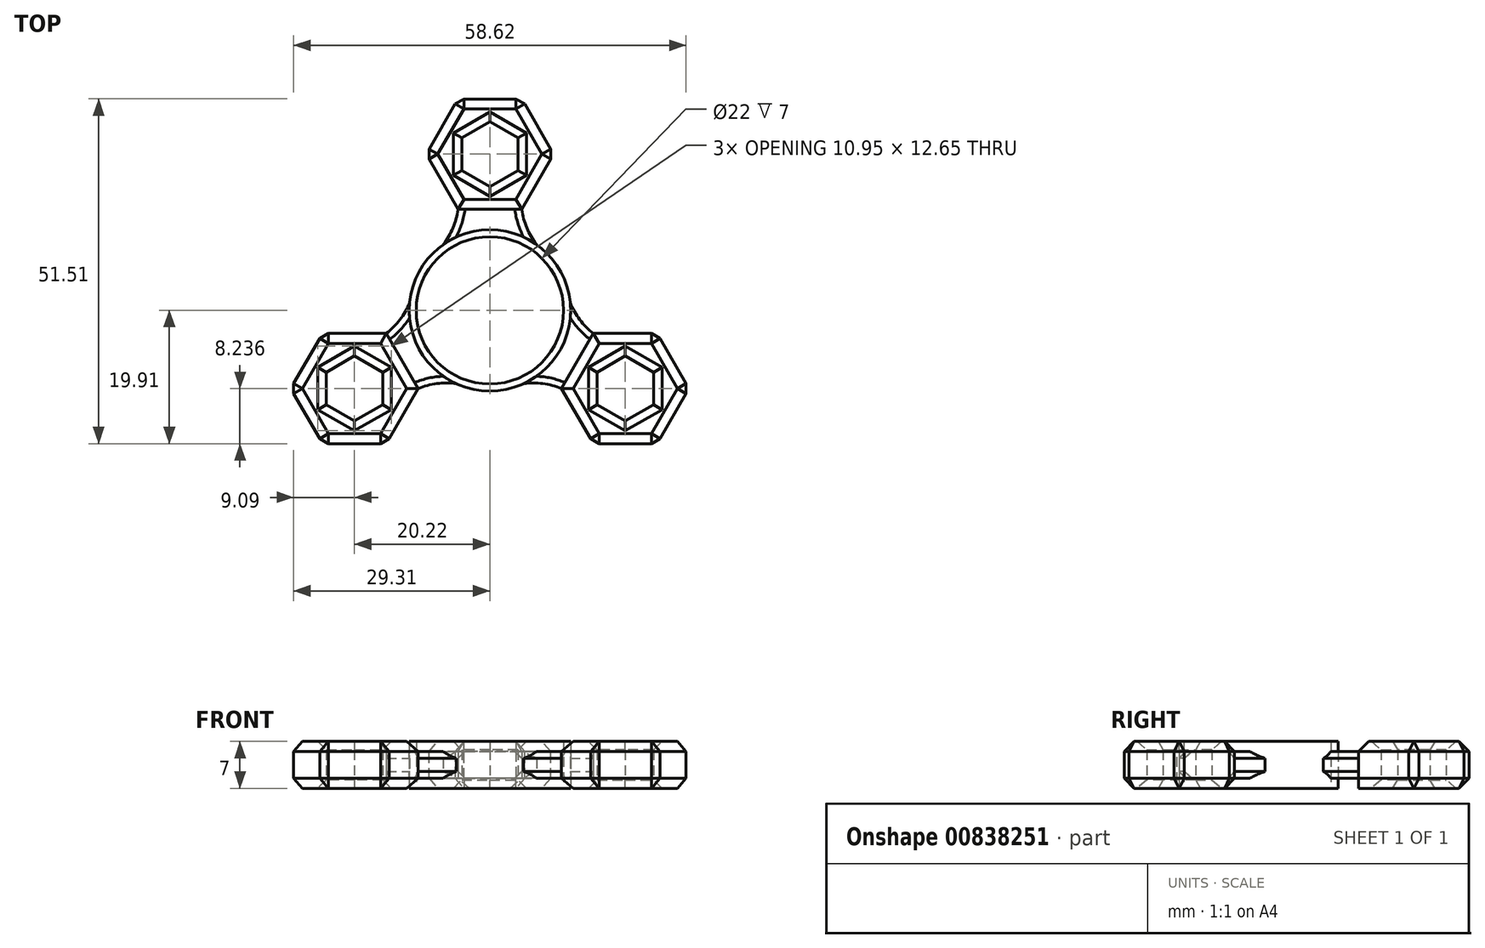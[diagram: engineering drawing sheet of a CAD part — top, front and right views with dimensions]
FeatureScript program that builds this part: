
annotation { "Feature Type Name" : "Feature", "Feature Type Description" : "" }
export const myFeature = defineFeature(function(context is Context, id is Id, definition is map)
    precondition{}
    {
        {
            var Q0;
            Q0=qCreatedBy(makeId("Top.planeOp"),FACE);
            var sketch = newSketch(context, id + "F0", { "sketchPlane" : qUnion([Q0])});
            skLineSegment(sketch, "E0", {"start": v(0, 31.6) * mm, "end": v(4.75, 31.6) * mm});
            skLineSegment(sketch, "E1.MirrorCS", {"start": v(0, 31.6) * mm, "end": v(-4.75, 31.6) * mm});
            skLineSegment(sketch, "E2", {"start": v(4.75, 31.6) * mm, "end": v(9.52, 23.35) * mm});
            skLineSegment(sketch, "E3.MirrorCS", {"start": v(-4.75, 31.6) * mm, "end": v(-9.52, 23.35) * mm});
            skLineSegment(sketch, "E4", {"start": v(9.52, 23.35) * mm, "end": v(4.75, 15.1) * mm});
            skLineSegment(sketch, "E5.MirrorCS", {"start": v(-9.52, 23.35) * mm, "end": v(-4.75, 15.1) * mm});
            skLineSegment(sketch, "E6.MirrorCS", {"start": v(0, 15.1) * mm, "end": v(4.75, 15.1) * mm});
            skLineSegment(sketch, "E7.MirrorCS", {"start": v(0, 15.1) * mm, "end": v(-4.75, 15.1) * mm});
            skLineSegment(sketch, "E8.MirrorCS", {"start": v(-13.08, -7.55) * mm, "end": v(-10.7, -11.67) * mm});
            skLineSegment(sketch, "E9.MirrorCS", {"start": v(-13.08, -7.55) * mm, "end": v(-15.45, -3.43) * mm});
            skLineSegment(sketch, "E10.MirrorCS", {"start": v(-24.98, -3.43) * mm, "end": v(-15.44, -3.43) * mm});
            skLineSegment(sketch, "E11.MirrorCS", {"start": v(-15.46, -19.91) * mm, "end": v(-10.7, -11.66) * mm});
            skLineSegment(sketch, "E12.MirrorCS", {"start": v(-24.99, -19.91) * mm, "end": v(-15.46, -19.91) * mm});
            skLineSegment(sketch, "E13.MirrorCS", {"start": v(-29.74, -11.68) * mm, "end": v(-24.98, -3.43) * mm});
            skLineSegment(sketch, "E14.MirrorCS", {"start": v(-27.36, -15.8) * mm, "end": v(-29.74, -11.68) * mm});
            skLineSegment(sketch, "E15.MirrorCS", {"start": v(-27.36, -15.8) * mm, "end": v(-24.99, -19.91) * mm});
            skLineSegment(sketch, "E16.MirrorCS", {"start": v(13.08, -7.55) * mm, "end": v(15.45, -3.43) * mm});
            skLineSegment(sketch, "E17.MirrorCS", {"start": v(13.08, -7.55) * mm, "end": v(10.7, -11.67) * mm});
            skLineSegment(sketch, "E18.MirrorCS", {"start": v(15.46, -19.91) * mm, "end": v(10.7, -11.66) * mm});
            skLineSegment(sketch, "E19.MirrorCS", {"start": v(24.98, -3.43) * mm, "end": v(15.44, -3.43) * mm});
            skLineSegment(sketch, "E20.MirrorCS", {"start": v(29.74, -11.68) * mm, "end": v(24.98, -3.43) * mm});
            skLineSegment(sketch, "E21.MirrorCS", {"start": v(27.36, -15.8) * mm, "end": v(29.74, -11.68) * mm});
            skLineSegment(sketch, "E22.MirrorCS", {"start": v(27.36, -15.8) * mm, "end": v(24.99, -19.91) * mm});
            skLineSegment(sketch, "E23.MirrorCS", {"start": v(24.99, -19.91) * mm, "end": v(15.46, -19.91) * mm});
            skLineSegment(sketch, "E24.0", {"start": v(-4.2, 25.78) * mm, "end": v(0, 28.2) * mm});
            skLineSegment(sketch, "E24.1", {"start": v(0, 28.2) * mm, "end": v(4.2, 25.78) * mm});
            skLineSegment(sketch, "E24.2", {"start": v(4.2, 25.78) * mm, "end": v(4.2, 20.92) * mm});
            skLineSegment(sketch, "E24.3", {"start": v(4.2, 20.92) * mm, "end": v(0, 18.5) * mm});
            skLineSegment(sketch, "E24.4", {"start": v(0, 18.5) * mm, "end": v(-4.2, 20.92) * mm});
            skLineSegment(sketch, "E24.5", {"start": v(-4.2, 20.92) * mm, "end": v(-4.2, 25.78) * mm});
            skPoint(sketch, "E24.0.midPoint", {"position": v(-2.1, 27) * mm});
            skLineSegment(sketch, "E25.MirrorCS", {"start": v(-16.01, -14.1) * mm, "end": v(-16.01, -9.25) * mm});
            skLineSegment(sketch, "E26.MirrorCS", {"start": v(-16.01, -9.25) * mm, "end": v(-20.22, -6.82) * mm});
            skLineSegment(sketch, "E27.MirrorCS", {"start": v(-20.22, -6.82) * mm, "end": v(-24.43, -9.25) * mm});
            skLineSegment(sketch, "E28.MirrorCS", {"start": v(-24.43, -9.25) * mm, "end": v(-24.43, -14.1) * mm});
            skLineSegment(sketch, "E29.MirrorCS", {"start": v(-24.43, -14.1) * mm, "end": v(-20.22, -16.53) * mm});
            skLineSegment(sketch, "E30.MirrorCS", {"start": v(-20.22, -16.53) * mm, "end": v(-16.01, -14.1) * mm});
            skLineSegment(sketch, "E31.MirrorCS", {"start": v(16.01, -9.25) * mm, "end": v(20.22, -6.82) * mm});
            skLineSegment(sketch, "E32.MirrorCS", {"start": v(16.01, -14.1) * mm, "end": v(16.01, -9.25) * mm});
            skLineSegment(sketch, "E33.MirrorCS", {"start": v(20.22, -16.53) * mm, "end": v(16.01, -14.1) * mm});
            skLineSegment(sketch, "E34.MirrorCS", {"start": v(24.43, -14.1) * mm, "end": v(20.22, -16.53) * mm});
            skLineSegment(sketch, "E35.MirrorCS", {"start": v(24.43, -9.25) * mm, "end": v(24.43, -14.1) * mm});
            skLineSegment(sketch, "E36.MirrorCS", {"start": v(20.22, -6.82) * mm, "end": v(24.43, -9.25) * mm});
            skCircle(sketch, "E37", {"center": v(0, 0) * mm, "radius": 11 * mm});
            skCircle(sketch, "E38", {"center": v(0, 0) * mm, "radius": 12.05 * mm});
            skArc(sketch, "E39", {"start": v(4.75, 15.1) * mm, "mid": v(5.52, 12.32) * mm, "end": v(6.97, 9.83) * mm});
            skArc(sketch, "E40.MirrorCS", {"start": v(-4.75, 15.1) * mm, "mid": v(-5.52, 12.32) * mm, "end": v(-6.97, 9.83) * mm});
            skArc(sketch, "E41.MirrorCS", {"start": v(-10.7, -11.67) * mm, "mid": v(-7.91, -10.94) * mm, "end": v(-5.03, -10.95) * mm});
            skArc(sketch, "E42.MirrorCS", {"start": v(-15.45, -3.43) * mm, "mid": v(-13.43, -1.38) * mm, "end": v(-12, 1.12) * mm});
            skArc(sketch, "E43.MirrorCS", {"start": v(15.45, -3.43) * mm, "mid": v(13.43, -1.38) * mm, "end": v(12, 1.12) * mm});
            skArc(sketch, "E44.MirrorCS", {"start": v(10.7, -11.67) * mm, "mid": v(7.91, -10.94) * mm, "end": v(5.03, -10.95) * mm});
            skSolve(sketch);
        }
        {
            var Q0;
            Q0=makeQuery(id+"F0.imprint","IMPRINT",FACE,{"disambiguationData":[TD([[makeQuery(id+"F0.imprint","IMPRINT",EDGE,{"derivedFrom":sQuery(id+"F0.wireOp",EDGE,"E0")}),-1.0]])]});
            var Q1;
            {var subQ4=sQuery(id+"F0.wireOp",EDGE,"E16.MirrorCS");Q1=makeQuery(id+"F0.imprint","IMPRINT",FACE,{"disambiguationData":[TD([[makeQuery(id+"F0.imprint","IMPRINT",EDGE,{"derivedFrom":subQ4}),-1.0]])]});}
            var Q2;
            {var subQ2=sQuery(id+"F0.wireOp",EDGE,"E8.MirrorCS");Q2=makeQuery(id+"F0.imprint","IMPRINT",FACE,{"disambiguationData":[TD([[makeQuery(id+"F0.imprint","IMPRINT",EDGE,{"derivedFrom":subQ2}),-1.0]])]});}
            var Q3;
            Q3=makeQuery(id+"F0.imprint","IMPRINT",FACE,{"disambiguationData":[TD([[makeQuery(id+"F0.imprint","IMPRINT",EDGE,{"derivedFrom":sQuery(id+"F0.wireOp",EDGE,"xe7wqnzr-XKuB-rW0O-xTz1-b7jerHm42rLD")}),-1.0]])]});
            extrude(context, id + "F1", {"entities" : qUnion([Q0, Q1, Q2, Q3]), "depth" : 7 * mm, "offsetDistance" : 25.4 * mm});
        }
        {
            var Q0;
            Q0=makeQuery(id+"F0.imprint","IMPRINT",FACE,{"disambiguationData":[TD([[makeQuery(id+"F0.imprint","IMPRINT",EDGE,{"derivedFrom":sQuery(id+"F0.wireOp",EDGE,"E16.MirrorCS")}),1.0]])]});
            var Q1;
            Q1=makeQuery(id+"F0.imprint","IMPRINT",FACE,{"disambiguationData":[TD([[makeQuery(id+"F0.imprint","IMPRINT",EDGE,{"derivedFrom":sQuery(id+"F0.wireOp",EDGE,"E8.MirrorCS")}),1.0]])]});
            var Q2;
            Q2=makeQuery(id+"F0.imprint","IMPRINT",FACE,{"disambiguationData":[TD([[makeQuery(id+"F0.imprint","IMPRINT",EDGE,{"derivedFrom":sQuery(id+"F0.wireOp",EDGE,"E6.MirrorCS")}),-1.0]])]});
            extrude(context, id + "F2", {"entities" : qUnion([Q0, Q1, Q2]), "depth" : 4 * mm, "offsetDistance" : 25.4 * mm});
        }
        {
            var Q0;
            Q0=makeQuery(id+"F2.opExtrude","SWEPT_BODY",BODY,{"disambiguationData":[OSD([sQuery(id+"F0.wireOp",EDGE,"vPjK45c8-EVP7-AFoe-6fc5-zKXZbxQBUroo"),sQuery(id+"F0.wireOp",EDGE,"E8.MirrorCS"),sQuery(id+"F0.wireOp",EDGE,"E9.MirrorCS"),sQuery(id+"F0.wireOp",EDGE,"01c6eca7-8cec-47bf-bf10-1e8c1c321e7b0.MirrorCS"),sQuery(id+"F0.wireOp",EDGE,"d1bce0d9-914a-43dd-a102-95f5fd3e93660.MirrorCS")])]});
            var Q1;
            Q1=makeQuery(id+"F2.opExtrude","SWEPT_BODY",BODY,{"disambiguationData":[OSD([sQuery(id+"F0.wireOp",EDGE,"vPjK45c8-EVP7-AFoe-6fc5-zKXZbxQBUroo"),sQuery(id+"F0.wireOp",EDGE,"E6.MirrorCS"),sQuery(id+"F0.wireOp",EDGE,"E7.MirrorCS"),sQuery(id+"F0.wireOp",EDGE,"E15wmxCf-tLpu-X0cc-KYuK-EZGoAjTdYror"),sQuery(id+"F0.wireOp",EDGE,"b77f33ba-465c-4afd-8519-29dd17539a6f0.MirrorCS")])]});
            var Q2;
            Q2=makeQuery(id+"F2.opExtrude","SWEPT_BODY",BODY,{"disambiguationData":[OSD([sQuery(id+"F0.wireOp",EDGE,"vPjK45c8-EVP7-AFoe-6fc5-zKXZbxQBUroo"),sQuery(id+"F0.wireOp",EDGE,"E16.MirrorCS"),sQuery(id+"F0.wireOp",EDGE,"E17.MirrorCS"),sQuery(id+"F0.wireOp",EDGE,"b3ed12b7-8768-48b8-8f4e-18517871a5bf0.MirrorCS"),sQuery(id+"F0.wireOp",EDGE,"d635de01-bb5d-4376-a8ab-b6ab56e229920.MirrorCS")])]});
            transform(context, id + "F3", {"entities" : qUnion([Q0, Q1, Q2]), "transformType" : TransformType.TRANSLATION_3D, "dx" : 0 * mm, "dy" : 0 * mm, "dz" : 1.5 * mm, "makeCopy" : false});
        }
        {
            var Q0;
            Q0=makeQuery(id+"F2.opExtrude","CAP_EDGE",EDGE,{"disambiguationData":[OSD([sQuery(id+"F0.wireOp",EDGE,"b77f33ba-465c-4afd-8519-29dd17539a6f0.MirrorCS")])],"isStart":false});
            var Q1;
            Q1=makeQuery(id+"F2.opExtrude","CAP_EDGE",EDGE,{"disambiguationData":[OSD([sQuery(id+"F0.wireOp",EDGE,"b77f33ba-465c-4afd-8519-29dd17539a6f0.MirrorCS")])],"isStart":true});
            var Q2;
            Q2=makeQuery(id+"F2.opExtrude","CAP_EDGE",EDGE,{"disambiguationData":[OSD([sQuery(id+"F0.wireOp",EDGE,"E15wmxCf-tLpu-X0cc-KYuK-EZGoAjTdYror")])],"isStart":false});
            var Q3;
            Q3=makeQuery(id+"F2.opExtrude","CAP_EDGE",EDGE,{"disambiguationData":[OSD([sQuery(id+"F0.wireOp",EDGE,"E15wmxCf-tLpu-X0cc-KYuK-EZGoAjTdYror")])],"isStart":true});
            var Q4;
            Q4=makeQuery(id+"F2.opExtrude","CAP_EDGE",EDGE,{"disambiguationData":[OSD([sQuery(id+"F0.wireOp",EDGE,"b3ed12b7-8768-48b8-8f4e-18517871a5bf0.MirrorCS")])],"isStart":true});
            var Q5;
            Q5=makeQuery(id+"F2.opExtrude","CAP_EDGE",EDGE,{"disambiguationData":[OSD([sQuery(id+"F0.wireOp",EDGE,"b3ed12b7-8768-48b8-8f4e-18517871a5bf0.MirrorCS")])],"isStart":false});
            var Q6;
            Q6=makeQuery(id+"F2.opExtrude","CAP_EDGE",EDGE,{"disambiguationData":[OSD([sQuery(id+"F0.wireOp",EDGE,"d635de01-bb5d-4376-a8ab-b6ab56e229920.MirrorCS")])],"isStart":false});
            var Q7;
            Q7=makeQuery(id+"F2.opExtrude","CAP_EDGE",EDGE,{"disambiguationData":[OSD([sQuery(id+"F0.wireOp",EDGE,"d635de01-bb5d-4376-a8ab-b6ab56e229920.MirrorCS")])],"isStart":true});
            var Q8;
            Q8=makeQuery(id+"F2.opExtrude","CAP_EDGE",EDGE,{"disambiguationData":[OSD([sQuery(id+"F0.wireOp",EDGE,"01c6eca7-8cec-47bf-bf10-1e8c1c321e7b0.MirrorCS")])],"isStart":true});
            var Q9;
            Q9=makeQuery(id+"F2.opExtrude","CAP_EDGE",EDGE,{"disambiguationData":[OSD([sQuery(id+"F0.wireOp",EDGE,"01c6eca7-8cec-47bf-bf10-1e8c1c321e7b0.MirrorCS")])],"isStart":false});
            var Q10;
            Q10=makeQuery(id+"F2.opExtrude","CAP_EDGE",EDGE,{"disambiguationData":[OSD([sQuery(id+"F0.wireOp",EDGE,"d1bce0d9-914a-43dd-a102-95f5fd3e93660.MirrorCS")])],"isStart":true});
            var Q11;
            Q11=makeQuery(id+"F2.opExtrude","CAP_EDGE",EDGE,{"disambiguationData":[OSD([sQuery(id+"F0.wireOp",EDGE,"d1bce0d9-914a-43dd-a102-95f5fd3e93660.MirrorCS")])],"isStart":false});
            var Q12;
            Q12=makeQuery(id+"F1.opExtrude","CAP_EDGE",EDGE,{"disambiguationData":[OSD([sQuery(id+"F0.wireOp",EDGE,"E16.MirrorCS"),sQuery(id+"F0.wireOp",EDGE,"E17.MirrorCS")])],"isStart":false});
            var Q13;
            Q13=makeQuery(id+"F1.opExtrude","CAP_EDGE",EDGE,{"disambiguationData":[OSD([sQuery(id+"F0.wireOp",EDGE,"E18.MirrorCS")])],"isStart":false});
            var Q14;
            Q14=makeQuery(id+"F1.opExtrude","CAP_EDGE",EDGE,{"disambiguationData":[OSD([sQuery(id+"F0.wireOp",EDGE,"E23.MirrorCS")])],"isStart":false});
            var Q15;
            Q15=makeQuery(id+"F1.opExtrude","CAP_EDGE",EDGE,{"disambiguationData":[OSD([sQuery(id+"F0.wireOp",EDGE,"E21.MirrorCS"),sQuery(id+"F0.wireOp",EDGE,"E22.MirrorCS")])],"isStart":false});
            var Q16;
            Q16=makeQuery(id+"F1.opExtrude","CAP_EDGE",EDGE,{"disambiguationData":[OSD([sQuery(id+"F0.wireOp",EDGE,"E19.MirrorCS")])],"isStart":false});
            var Q17;
            Q17=makeQuery(id+"F1.opExtrude","CAP_EDGE",EDGE,{"disambiguationData":[OSD([sQuery(id+"F0.wireOp",EDGE,"E20.MirrorCS")])],"isStart":false});
            var Q18;
            Q18=makeQuery(id+"F1.opExtrude","CAP_EDGE",EDGE,{"disambiguationData":[OSD([sQuery(id+"F0.wireOp",EDGE,"E4")])],"isStart":false});
            var Q19;
            Q19=makeQuery(id+"F1.opExtrude","CAP_EDGE",EDGE,{"disambiguationData":[OSD([sQuery(id+"F0.wireOp",EDGE,"E2")])],"isStart":false});
            var Q20;
            Q20=makeQuery(id+"F1.opExtrude","CAP_EDGE",EDGE,{"disambiguationData":[OSD([sQuery(id+"F0.wireOp",EDGE,"E6.MirrorCS"),sQuery(id+"F0.wireOp",EDGE,"E7.MirrorCS")])],"isStart":false});
            var Q21;
            Q21=makeQuery(id+"F1.opExtrude","CAP_EDGE",EDGE,{"disambiguationData":[OSD([sQuery(id+"F0.wireOp",EDGE,"E5.MirrorCS")])],"isStart":false});
            var Q22;
            Q22=makeQuery(id+"F1.opExtrude","CAP_EDGE",EDGE,{"disambiguationData":[OSD([sQuery(id+"F0.wireOp",EDGE,"E3.MirrorCS")])],"isStart":false});
            var Q23;
            Q23=makeQuery(id+"F1.opExtrude","CAP_EDGE",EDGE,{"disambiguationData":[OSD([sQuery(id+"F0.wireOp",EDGE,"E0"),sQuery(id+"F0.wireOp",EDGE,"E1.MirrorCS")])],"isStart":false});
            var Q24;
            Q24=makeQuery(id+"F1.opExtrude","CAP_EDGE",EDGE,{"disambiguationData":[OSD([sQuery(id+"F0.wireOp",EDGE,"E10.MirrorCS")])],"isStart":false});
            var Q25;
            Q25=makeQuery(id+"F1.opExtrude","CAP_EDGE",EDGE,{"disambiguationData":[OSD([sQuery(id+"F0.wireOp",EDGE,"E13.MirrorCS")])],"isStart":false});
            var Q26;
            Q26=makeQuery(id+"F1.opExtrude","CAP_EDGE",EDGE,{"disambiguationData":[OSD([sQuery(id+"F0.wireOp",EDGE,"E14.MirrorCS"),sQuery(id+"F0.wireOp",EDGE,"E15.MirrorCS")])],"isStart":false});
            var Q27;
            Q27=makeQuery(id+"F1.opExtrude","CAP_EDGE",EDGE,{"disambiguationData":[OSD([sQuery(id+"F0.wireOp",EDGE,"E12.MirrorCS")])],"isStart":false});
            var Q28;
            Q28=makeQuery(id+"F1.opExtrude","CAP_EDGE",EDGE,{"disambiguationData":[OSD([sQuery(id+"F0.wireOp",EDGE,"E11.MirrorCS")])],"isStart":false});
            var Q29;
            Q29=makeQuery(id+"F1.opExtrude","CAP_EDGE",EDGE,{"disambiguationData":[OSD([sQuery(id+"F0.wireOp",EDGE,"E8.MirrorCS"),sQuery(id+"F0.wireOp",EDGE,"E9.MirrorCS")])],"isStart":false});
            var Q30;
            Q30=makeQuery(id+"F1.opExtrude","CAP_EDGE",EDGE,{"disambiguationData":[OSD([sQuery(id+"F0.wireOp",EDGE,"E18.MirrorCS")])],"isStart":true});
            var Q31;
            Q31=makeQuery(id+"F1.opExtrude","CAP_EDGE",EDGE,{"disambiguationData":[OSD([sQuery(id+"F0.wireOp",EDGE,"E23.MirrorCS")])],"isStart":true});
            var Q32;
            Q32=makeQuery(id+"F1.opExtrude","CAP_EDGE",EDGE,{"disambiguationData":[OSD([sQuery(id+"F0.wireOp",EDGE,"E16.MirrorCS"),sQuery(id+"F0.wireOp",EDGE,"E17.MirrorCS")])],"isStart":true});
            var Q33;
            Q33=makeQuery(id+"F1.opExtrude","CAP_EDGE",EDGE,{"disambiguationData":[OSD([sQuery(id+"F0.wireOp",EDGE,"E21.MirrorCS"),sQuery(id+"F0.wireOp",EDGE,"E22.MirrorCS")])],"isStart":true});
            var Q34;
            Q34=makeQuery(id+"F1.opExtrude","CAP_EDGE",EDGE,{"disambiguationData":[OSD([sQuery(id+"F0.wireOp",EDGE,"E20.MirrorCS")])],"isStart":true});
            var Q35;
            Q35=makeQuery(id+"F1.opExtrude","CAP_EDGE",EDGE,{"disambiguationData":[OSD([sQuery(id+"F0.wireOp",EDGE,"E19.MirrorCS")])],"isStart":true});
            var Q36;
            Q36=makeQuery(id+"F1.opExtrude","SWEPT_EDGE",EDGE,{"disambiguationData":[OSD([sQuery(id+"F0.wireOp",EDGE,"E23.MirrorCS"),sQuery(id+"F0.wireOp",EDGE,"E18.MirrorCS")])]});
            var Q37;
            Q37=makeQuery(id+"F1.opExtrude","SWEPT_EDGE",EDGE,{"disambiguationData":[OSD([sQuery(id+"F0.wireOp",EDGE,"E22.MirrorCS"),sQuery(id+"F0.wireOp",EDGE,"E23.MirrorCS")])]});
            var Q38;
            Q38=makeQuery(id+"F1.opExtrude","SWEPT_EDGE",EDGE,{"disambiguationData":[OSD([sQuery(id+"F0.wireOp",EDGE,"E20.MirrorCS"),sQuery(id+"F0.wireOp",EDGE,"E21.MirrorCS")])]});
            var Q39;
            Q39=makeQuery(id+"F1.opExtrude","SWEPT_EDGE",EDGE,{"disambiguationData":[OSD([sQuery(id+"F0.wireOp",EDGE,"E19.MirrorCS"),sQuery(id+"F0.wireOp",EDGE,"E20.MirrorCS")])]});
            var Q40;
            Q40=makeQuery(id+"F1.opExtrude","CAP_EDGE",EDGE,{"disambiguationData":[OSD([sQuery(id+"F0.wireOp",EDGE,"E8.MirrorCS"),sQuery(id+"F0.wireOp",EDGE,"E9.MirrorCS")])],"isStart":true});
            var Q41;
            Q41=makeQuery(id+"F1.opExtrude","CAP_EDGE",EDGE,{"disambiguationData":[OSD([sQuery(id+"F0.wireOp",EDGE,"E11.MirrorCS")])],"isStart":true});
            var Q42;
            Q42=makeQuery(id+"F1.opExtrude","CAP_EDGE",EDGE,{"disambiguationData":[OSD([sQuery(id+"F0.wireOp",EDGE,"E12.MirrorCS")])],"isStart":true});
            var Q43;
            Q43=makeQuery(id+"F1.opExtrude","CAP_EDGE",EDGE,{"disambiguationData":[OSD([sQuery(id+"F0.wireOp",EDGE,"E14.MirrorCS"),sQuery(id+"F0.wireOp",EDGE,"E15.MirrorCS")])],"isStart":true});
            var Q44;
            Q44=makeQuery(id+"F1.opExtrude","CAP_EDGE",EDGE,{"disambiguationData":[OSD([sQuery(id+"F0.wireOp",EDGE,"E13.MirrorCS")])],"isStart":true});
            var Q45;
            Q45=makeQuery(id+"F1.opExtrude","CAP_EDGE",EDGE,{"disambiguationData":[OSD([sQuery(id+"F0.wireOp",EDGE,"E10.MirrorCS")])],"isStart":true});
            var Q46;
            Q46=makeQuery(id+"F1.opExtrude","SWEPT_EDGE",EDGE,{"disambiguationData":[OSD([sQuery(id+"F0.wireOp",EDGE,"E11.MirrorCS"),sQuery(id+"F0.wireOp",EDGE,"E12.MirrorCS")])]});
            var Q47;
            Q47=makeQuery(id+"F1.opExtrude","SWEPT_EDGE",EDGE,{"disambiguationData":[OSD([sQuery(id+"F0.wireOp",EDGE,"E12.MirrorCS"),sQuery(id+"F0.wireOp",EDGE,"E15.MirrorCS")])]});
            var Q48;
            Q48=makeQuery(id+"F1.opExtrude","SWEPT_EDGE",EDGE,{"disambiguationData":[OSD([sQuery(id+"F0.wireOp",EDGE,"E13.MirrorCS"),sQuery(id+"F0.wireOp",EDGE,"E14.MirrorCS")])]});
            var Q49;
            Q49=makeQuery(id+"F1.opExtrude","SWEPT_EDGE",EDGE,{"disambiguationData":[OSD([sQuery(id+"F0.wireOp",EDGE,"E3.MirrorCS"),sQuery(id+"F0.wireOp",EDGE,"E5.MirrorCS")])]});
            var Q50;
            Q50=makeQuery(id+"F1.opExtrude","SWEPT_EDGE",EDGE,{"disambiguationData":[OSD([sQuery(id+"F0.wireOp",EDGE,"E1.MirrorCS"),sQuery(id+"F0.wireOp",EDGE,"E3.MirrorCS")])]});
            var Q51;
            Q51=makeQuery(id+"F1.opExtrude","SWEPT_EDGE",EDGE,{"disambiguationData":[OSD([sQuery(id+"F0.wireOp",EDGE,"E0"),sQuery(id+"F0.wireOp",EDGE,"E2")])]});
            var Q52;
            Q52=makeQuery(id+"F1.opExtrude","CAP_EDGE",EDGE,{"disambiguationData":[OSD([sQuery(id+"F0.wireOp",EDGE,"E0"),sQuery(id+"F0.wireOp",EDGE,"E1.MirrorCS")])],"isStart":true});
            var Q53;
            Q53=makeQuery(id+"F1.opExtrude","CAP_EDGE",EDGE,{"disambiguationData":[OSD([sQuery(id+"F0.wireOp",EDGE,"E3.MirrorCS")])],"isStart":true});
            var Q54;
            Q54=makeQuery(id+"F1.opExtrude","CAP_EDGE",EDGE,{"disambiguationData":[OSD([sQuery(id+"F0.wireOp",EDGE,"E5.MirrorCS")])],"isStart":true});
            var Q55;
            Q55=makeQuery(id+"F1.opExtrude","SWEPT_EDGE",EDGE,{"disambiguationData":[OSD([sQuery(id+"F0.wireOp",EDGE,"E2"),sQuery(id+"F0.wireOp",EDGE,"E4")])]});
            var Q56;
            Q56=makeQuery(id+"F1.opExtrude","CAP_EDGE",EDGE,{"disambiguationData":[OSD([sQuery(id+"F0.wireOp",EDGE,"E2")])],"isStart":true});
            var Q57;
            Q57=makeQuery(id+"F1.opExtrude","CAP_EDGE",EDGE,{"disambiguationData":[OSD([sQuery(id+"F0.wireOp",EDGE,"E4")])],"isStart":true});
            var Q58;
            Q58=makeQuery(id+"F1.opExtrude","SWEPT_EDGE",EDGE,{"disambiguationData":[OSD([sQuery(id+"F0.wireOp",EDGE,"E10.MirrorCS"),sQuery(id+"F0.wireOp",EDGE,"E13.MirrorCS")])]});
            chamfer(context, id + "F4", {"entities" : qUnion([Q0, Q1, Q2, Q3, Q4, Q5, Q6, Q7, Q8, Q9, Q10, Q11, Q12, Q13, Q14, Q15, Q16, Q17, Q18, Q19, Q20, Q21, Q22, Q23, Q24, Q25, Q26, Q27, Q28, Q29, Q30, Q31, Q32, Q33, Q34, Q35, Q36, Q37, Q38, Q39, Q40, Q41, Q42, Q43, Q44, Q45, Q46, Q47, Q48, Q49, Q50, Q51, Q52, Q53, Q54, Q55, Q56, Q57, Q58]), "width" : 1.5 * mm, "tangentPropagation" : true});
        }
        {
            var Q0;
            Q0=makeQuery(id+"F1.opExtrude","CAP_EDGE",EDGE,{"disambiguationData":[OSD([sQuery(id+"F0.wireOp",EDGE,"E31.MirrorCS")])],"isStart":true});
            var Q1;
            Q1=makeQuery(id+"F1.opExtrude","CAP_EDGE",EDGE,{"disambiguationData":[OSD([sQuery(id+"F0.wireOp",EDGE,"E36.MirrorCS")])],"isStart":true});
            var Q2;
            Q2=makeQuery(id+"F1.opExtrude","CAP_EDGE",EDGE,{"disambiguationData":[OSD([sQuery(id+"F0.wireOp",EDGE,"E31.MirrorCS")])],"isStart":false});
            var Q3;
            Q3=makeQuery(id+"F1.opExtrude","CAP_EDGE",EDGE,{"disambiguationData":[OSD([sQuery(id+"F0.wireOp",EDGE,"E36.MirrorCS")])],"isStart":false});
            var Q4;
            Q4=makeQuery(id+"F1.opExtrude","CAP_EDGE",EDGE,{"disambiguationData":[OSD([sQuery(id+"F0.wireOp",EDGE,"E32.MirrorCS")])],"isStart":true});
            var Q5;
            Q5=makeQuery(id+"F1.opExtrude","CAP_EDGE",EDGE,{"disambiguationData":[OSD([sQuery(id+"F0.wireOp",EDGE,"E32.MirrorCS")])],"isStart":false});
            var Q6;
            Q6=makeQuery(id+"F1.opExtrude","CAP_EDGE",EDGE,{"disambiguationData":[OSD([sQuery(id+"F0.wireOp",EDGE,"E35.MirrorCS")])],"isStart":false});
            var Q7;
            Q7=makeQuery(id+"F1.opExtrude","CAP_EDGE",EDGE,{"disambiguationData":[OSD([sQuery(id+"F0.wireOp",EDGE,"E35.MirrorCS")])],"isStart":true});
            var Q8;
            Q8=makeQuery(id+"F1.opExtrude","CAP_EDGE",EDGE,{"disambiguationData":[OSD([sQuery(id+"F0.wireOp",EDGE,"E34.MirrorCS")])],"isStart":false});
            var Q9;
            Q9=makeQuery(id+"F1.opExtrude","CAP_EDGE",EDGE,{"disambiguationData":[OSD([sQuery(id+"F0.wireOp",EDGE,"E33.MirrorCS")])],"isStart":false});
            var Q10;
            Q10=makeQuery(id+"F1.opExtrude","CAP_EDGE",EDGE,{"disambiguationData":[OSD([sQuery(id+"F0.wireOp",EDGE,"E34.MirrorCS")])],"isStart":true});
            var Q11;
            Q11=makeQuery(id+"F1.opExtrude","CAP_EDGE",EDGE,{"disambiguationData":[OSD([sQuery(id+"F0.wireOp",EDGE,"E33.MirrorCS")])],"isStart":true});
            var Q12;
            Q12=makeQuery(id+"F1.opExtrude","CAP_EDGE",EDGE,{"disambiguationData":[OSD([sQuery(id+"F0.wireOp",EDGE,"E29.MirrorCS")])],"isStart":true});
            var Q13;
            Q13=makeQuery(id+"F1.opExtrude","CAP_EDGE",EDGE,{"disambiguationData":[OSD([sQuery(id+"F0.wireOp",EDGE,"E30.MirrorCS")])],"isStart":true});
            var Q14;
            Q14=makeQuery(id+"F1.opExtrude","CAP_EDGE",EDGE,{"disambiguationData":[OSD([sQuery(id+"F0.wireOp",EDGE,"E25.MirrorCS")])],"isStart":true});
            var Q15;
            Q15=makeQuery(id+"F1.opExtrude","CAP_EDGE",EDGE,{"disambiguationData":[OSD([sQuery(id+"F0.wireOp",EDGE,"E26.MirrorCS")])],"isStart":false});
            var Q16;
            Q16=makeQuery(id+"F1.opExtrude","CAP_EDGE",EDGE,{"disambiguationData":[OSD([sQuery(id+"F0.wireOp",EDGE,"E25.MirrorCS")])],"isStart":false});
            var Q17;
            Q17=makeQuery(id+"F1.opExtrude","CAP_EDGE",EDGE,{"disambiguationData":[OSD([sQuery(id+"F0.wireOp",EDGE,"E30.MirrorCS")])],"isStart":false});
            var Q18;
            Q18=makeQuery(id+"F1.opExtrude","CAP_EDGE",EDGE,{"disambiguationData":[OSD([sQuery(id+"F0.wireOp",EDGE,"E29.MirrorCS")])],"isStart":false});
            var Q19;
            Q19=makeQuery(id+"F1.opExtrude","CAP_EDGE",EDGE,{"disambiguationData":[OSD([sQuery(id+"F0.wireOp",EDGE,"E28.MirrorCS")])],"isStart":true});
            var Q20;
            Q20=makeQuery(id+"F1.opExtrude","CAP_EDGE",EDGE,{"disambiguationData":[OSD([sQuery(id+"F0.wireOp",EDGE,"E28.MirrorCS")])],"isStart":false});
            var Q21;
            Q21=makeQuery(id+"F1.opExtrude","CAP_EDGE",EDGE,{"disambiguationData":[OSD([sQuery(id+"F0.wireOp",EDGE,"E27.MirrorCS")])],"isStart":false});
            var Q22;
            Q22=makeQuery(id+"F1.opExtrude","CAP_EDGE",EDGE,{"disambiguationData":[OSD([sQuery(id+"F0.wireOp",EDGE,"E27.MirrorCS")])],"isStart":true});
            var Q23;
            Q23=makeQuery(id+"F1.opExtrude","CAP_EDGE",EDGE,{"disambiguationData":[OSD([sQuery(id+"F0.wireOp",EDGE,"E26.MirrorCS")])],"isStart":true});
            var Q24;
            Q24=makeQuery(id+"F1.opExtrude","CAP_EDGE",EDGE,{"disambiguationData":[OSD([sQuery(id+"F0.wireOp",EDGE,"E24.0")])],"isStart":true});
            var Q25;
            Q25=makeQuery(id+"F1.opExtrude","CAP_EDGE",EDGE,{"disambiguationData":[OSD([sQuery(id+"F0.wireOp",EDGE,"E24.0")])],"isStart":false});
            var Q26;
            Q26=makeQuery(id+"F1.opExtrude","CAP_EDGE",EDGE,{"disambiguationData":[OSD([sQuery(id+"F0.wireOp",EDGE,"E24.5")])],"isStart":false});
            var Q27;
            Q27=makeQuery(id+"F1.opExtrude","CAP_EDGE",EDGE,{"disambiguationData":[OSD([sQuery(id+"F0.wireOp",EDGE,"E24.5")])],"isStart":true});
            var Q28;
            Q28=makeQuery(id+"F1.opExtrude","CAP_EDGE",EDGE,{"disambiguationData":[OSD([sQuery(id+"F0.wireOp",EDGE,"E24.4")])],"isStart":false});
            var Q29;
            Q29=makeQuery(id+"F1.opExtrude","CAP_EDGE",EDGE,{"disambiguationData":[OSD([sQuery(id+"F0.wireOp",EDGE,"E24.4")])],"isStart":true});
            var Q30;
            Q30=makeQuery(id+"F1.opExtrude","CAP_EDGE",EDGE,{"disambiguationData":[OSD([sQuery(id+"F0.wireOp",EDGE,"E24.1")])],"isStart":true});
            var Q31;
            Q31=makeQuery(id+"F1.opExtrude","CAP_EDGE",EDGE,{"disambiguationData":[OSD([sQuery(id+"F0.wireOp",EDGE,"E24.1")])],"isStart":false});
            var Q32;
            Q32=makeQuery(id+"F1.opExtrude","CAP_EDGE",EDGE,{"disambiguationData":[OSD([sQuery(id+"F0.wireOp",EDGE,"E24.2")])],"isStart":true});
            var Q33;
            Q33=makeQuery(id+"F1.opExtrude","CAP_EDGE",EDGE,{"disambiguationData":[OSD([sQuery(id+"F0.wireOp",EDGE,"E24.2")])],"isStart":false});
            var Q34;
            Q34=makeQuery(id+"F1.opExtrude","CAP_EDGE",EDGE,{"disambiguationData":[OSD([sQuery(id+"F0.wireOp",EDGE,"E24.3")])],"isStart":false});
            var Q35;
            Q35=makeQuery(id+"F1.opExtrude","CAP_EDGE",EDGE,{"disambiguationData":[OSD([sQuery(id+"F0.wireOp",EDGE,"E24.3")])],"isStart":true});
            chamfer(context, id + "F5", {"entities" : qUnion([Q0, Q1, Q2, Q3, Q4, Q5, Q6, Q7, Q8, Q9, Q10, Q11, Q12, Q13, Q14, Q15, Q16, Q17, Q18, Q19, Q20, Q21, Q22, Q23, Q24, Q25, Q26, Q27, Q28, Q29, Q30, Q31, Q32, Q33, Q34, Q35]), "width" : 1.27 * mm, "tangentPropagation" : true});
        }
        {
            var Q0;
            Q0=makeQuery(id+"F0.imprint","IMPRINT",FACE,{"disambiguationData":[TD([[makeQuery(id+"F0.imprint","IMPRINT",EDGE,{"derivedFrom":sQuery(id+"F0.wireOp",EDGE,"E37")}),-1.0]])]});
            extrude(context, id + "F6", {"entities" : qUnion([Q0]), "depth" : 7 * mm, "offsetDistance" : 25.4 * mm});
        }
        {
            var Q0;
            Q0=makeQuery(id+"F2.opExtrude","CAP_EDGE",EDGE,{"disambiguationData":[OSD([sQuery(id+"F0.wireOp",EDGE,"E44.MirrorCS")])],"isStart":false});
            var Q1;
            Q1=makeQuery(id+"F2.opExtrude","CAP_EDGE",EDGE,{"disambiguationData":[OSD([sQuery(id+"F0.wireOp",EDGE,"E44.MirrorCS")])],"isStart":true});
            var Q2;
            Q2=makeQuery(id+"F2.opExtrude","CAP_EDGE",EDGE,{"disambiguationData":[OSD([sQuery(id+"F0.wireOp",EDGE,"E43.MirrorCS")])],"isStart":false});
            var Q3;
            Q3=makeQuery(id+"F2.opExtrude","CAP_EDGE",EDGE,{"disambiguationData":[OSD([sQuery(id+"F0.wireOp",EDGE,"E43.MirrorCS")])],"isStart":true});
            var Q4;
            Q4=makeQuery(id+"F2.opExtrude","CAP_EDGE",EDGE,{"disambiguationData":[OSD([sQuery(id+"F0.wireOp",EDGE,"E39")])],"isStart":true});
            var Q5;
            Q5=makeQuery(id+"F2.opExtrude","CAP_EDGE",EDGE,{"disambiguationData":[OSD([sQuery(id+"F0.wireOp",EDGE,"E39")])],"isStart":false});
            var Q6;
            Q6=makeQuery(id+"F2.opExtrude","CAP_EDGE",EDGE,{"disambiguationData":[OSD([sQuery(id+"F0.wireOp",EDGE,"E40.MirrorCS")])],"isStart":false});
            var Q7;
            Q7=makeQuery(id+"F2.opExtrude","CAP_EDGE",EDGE,{"disambiguationData":[OSD([sQuery(id+"F0.wireOp",EDGE,"E40.MirrorCS")])],"isStart":true});
            var Q8;
            Q8=makeQuery(id+"F2.opExtrude","CAP_EDGE",EDGE,{"disambiguationData":[OSD([sQuery(id+"F0.wireOp",EDGE,"E42.MirrorCS")])],"isStart":true});
            var Q9;
            Q9=makeQuery(id+"F2.opExtrude","CAP_EDGE",EDGE,{"disambiguationData":[OSD([sQuery(id+"F0.wireOp",EDGE,"E42.MirrorCS")])],"isStart":false});
            var Q10;
            Q10=makeQuery(id+"F2.opExtrude","CAP_EDGE",EDGE,{"disambiguationData":[OSD([sQuery(id+"F0.wireOp",EDGE,"E41.MirrorCS")])],"isStart":true});
            var Q11;
            Q11=makeQuery(id+"F2.opExtrude","CAP_EDGE",EDGE,{"disambiguationData":[OSD([sQuery(id+"F0.wireOp",EDGE,"E41.MirrorCS")])],"isStart":false});
            chamfer(context, id + "F7", {"entities" : qUnion([Q0, Q1, Q2, Q3, Q4, Q5, Q6, Q7, Q8, Q9, Q10, Q11]), "width" : 1.02 * mm, "tangentPropagation" : true});
        }
    });
